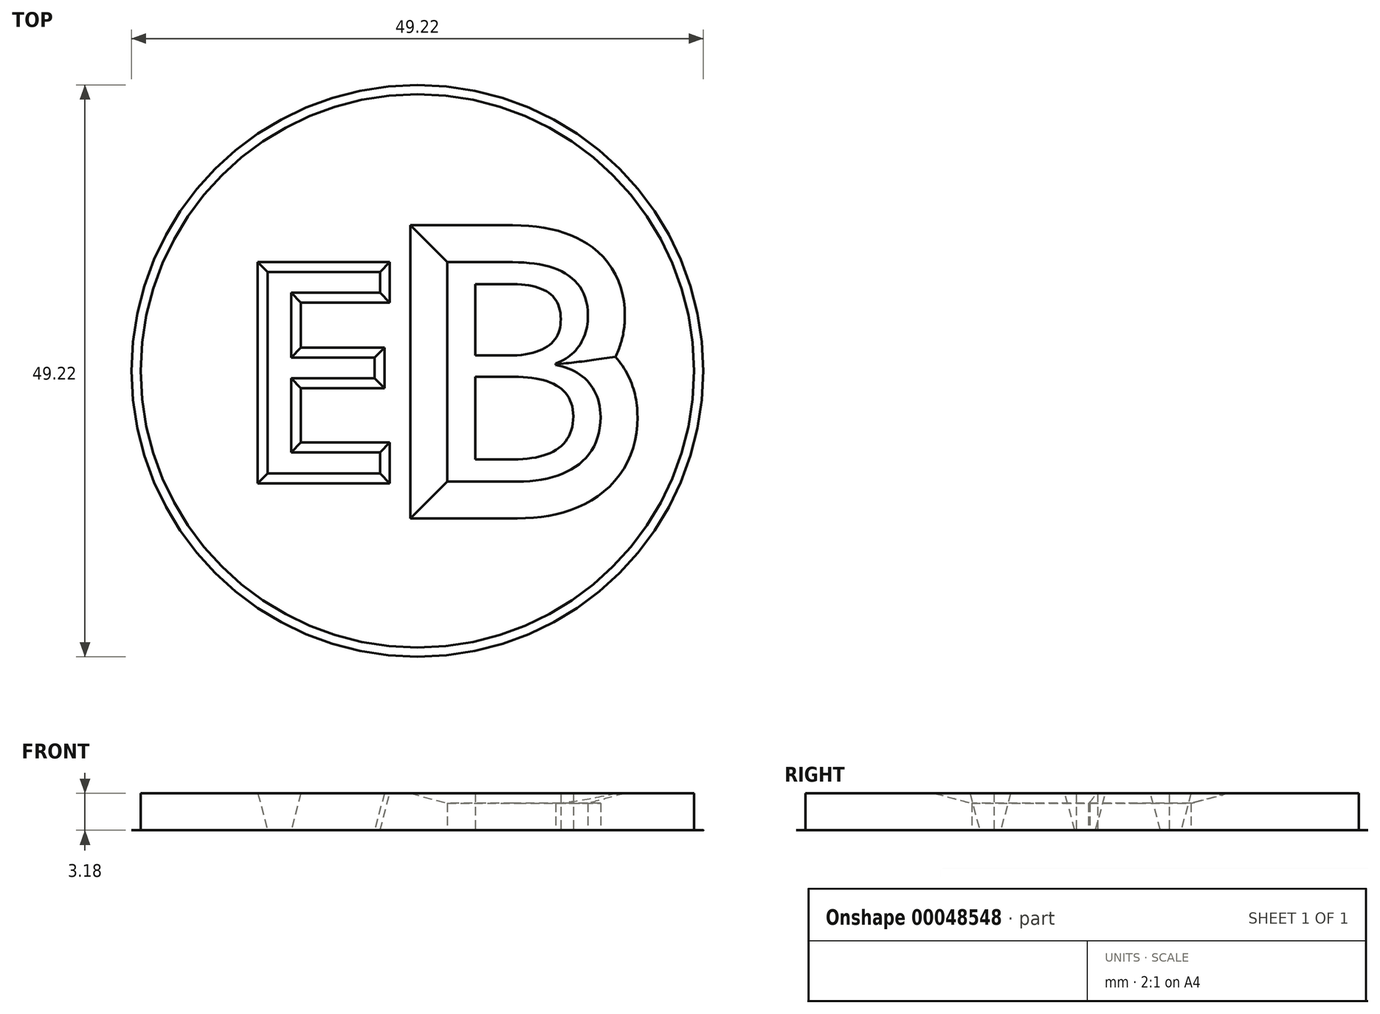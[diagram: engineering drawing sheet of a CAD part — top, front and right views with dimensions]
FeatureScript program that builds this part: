
annotation { "Feature Type Name" : "Feature", "Feature Type Description" : "" }
export const myFeature = defineFeature(function(context is Context, id is Id, definition is map)
    precondition{}
    {
        {
            var Q0;
            Q0=qCreatedBy(makeId("Top.planeOp"),FACE);
            var sketch = newSketch(context, id + "F0", { "sketchPlane" : qUnion([Q0])});
            skCircle(sketch, "E0", {"center": v(0, 0) * mm, "radius": 24.6 * mm});
            skSolve(sketch);
        }
        {
            var Q0;
            Q0=makeQuery(id+"F0.imprint","IMPRINT",FACE,{"disambiguationData":[TD([[makeQuery(id+"F0.imprint","IMPRINT",EDGE,{"derivedFrom":sQuery(id+"F0.wireOp",EDGE,"E0")}),1.0]])]});
            extrude(context, id + "F1", {"entities" : qUnion([Q0]), "depth" : 1 / 406.4 * mm});
        }
        {
            var Q0;
            Q0=qCreatedBy(makeId("Top.planeOp"),FACE);
            var sketch = newSketch(context, id + "F2", { "sketchPlane" : qUnion([Q0])});
            skCircle(sketch, "E1", {"center": v(0, 0) * mm, "radius": 23.81 * mm});
            skSolve(sketch);
        }
        {
            var Q0;
            Q0=qSketchRegion(id+"F2",true);
            extrude(context, id + "F3", {"entities" : qUnion([Q0]), "operationType" : NewBodyOperationType.ADD, "depth" : 3.17 * mm});
        }
        {
            var Q0;
            Q0=qCreatedBy(makeId("Top.planeOp"),FACE);
            var sketch = newSketch(context, id + "F4", { "sketchPlane" : qUnion([Q0])});
            skText(sketch, "E2", { "text": "E", "fontName": "OpenSans-Regular.ttf"});
            const initialGuessF4  = {"E2": [-0.01527, -0.00882, 1, 0, 0.01748]};
            skSetInitialGuess(sketch, initialGuessF4);
            skSolve(sketch);
        }
        {
            var Q0;
            Q0=qSketchRegion(id+"F4",true);
            var Q1;
            Q1=qSketchRegion(id+"Fgxxi4QDRaKe19X_1",true);
            extrude(context, id + "F5", {"entities" : qUnion([Q0, Q1]), "operationType" : NewBodyOperationType.REMOVE, "endBound" : BoundingType.THROUGH_ALL, "depth" : 25.4 * mm});
        }
        {
            var Q0;
            Q0=makeQuery(id+"F5.boolean.opBoolean","INTERSECT",EDGE,{"derivedFrom":[makeQuery(id+"F3.opExtrude","CAP_FACE",FACE,{"disambiguationData":[OSD([sQuery(id+"F2.wireOp",EDGE,"E1")])],"isStart":false}),makeQuery(id+"F5.opExtrude","SWEPT_FACE",FACE,{"disambiguationData":[OSD([sQuery(id+"F4.wireOp",EDGE,"E2.sketch_text.stroke-4")])]})]});
            var Q1;
            Q1=makeQuery(id+"F5.boolean.opBoolean","INTERSECT",EDGE,{"derivedFrom":[makeQuery(id+"F3.opExtrude","CAP_FACE",FACE,{"disambiguationData":[OSD([sQuery(id+"F2.wireOp",EDGE,"E1")])],"isStart":false}),makeQuery(id+"F5.opExtrude","SWEPT_FACE",FACE,{"disambiguationData":[OSD([sQuery(id+"F4.wireOp",EDGE,"E2.sketch_text.stroke-2")])]})]});
            var Q2;
            Q2=makeQuery(id+"F5.boolean.opBoolean","INTERSECT",EDGE,{"derivedFrom":[makeQuery(id+"F3.opExtrude","CAP_FACE",FACE,{"disambiguationData":[OSD([sQuery(id+"F2.wireOp",EDGE,"E1")])],"isStart":false}),makeQuery(id+"F5.opExtrude","SWEPT_FACE",FACE,{"disambiguationData":[OSD([sQuery(id+"F4.wireOp",EDGE,"E2.sketch_text.stroke-1")])]})]});
            var Q3;
            Q3=makeQuery(id+"F5.boolean.opBoolean","INTERSECT",EDGE,{"derivedFrom":[makeQuery(id+"F3.opExtrude","CAP_FACE",FACE,{"disambiguationData":[OSD([sQuery(id+"F2.wireOp",EDGE,"E1")])],"isStart":false}),makeQuery(id+"F5.opExtrude","SWEPT_FACE",FACE,{"disambiguationData":[OSD([sQuery(id+"F4.wireOp",EDGE,"E2.sketch_text.stroke-8")])]})]});
            var Q4;
            Q4=makeQuery(id+"F5.boolean.opBoolean","INTERSECT",EDGE,{"derivedFrom":[makeQuery(id+"F3.opExtrude","CAP_FACE",FACE,{"disambiguationData":[OSD([sQuery(id+"F2.wireOp",EDGE,"E1")])],"isStart":false}),makeQuery(id+"F5.opExtrude","SWEPT_FACE",FACE,{"disambiguationData":[OSD([sQuery(id+"F4.wireOp",EDGE,"E2.sketch_text.stroke-0")])]})]});
            var Q5;
            Q5=makeQuery(id+"F5.boolean.opBoolean","INTERSECT",EDGE,{"derivedFrom":[makeQuery(id+"F3.opExtrude","CAP_FACE",FACE,{"disambiguationData":[OSD([sQuery(id+"F2.wireOp",EDGE,"E1")])],"isStart":false}),makeQuery(id+"F5.opExtrude","SWEPT_FACE",FACE,{"disambiguationData":[OSD([sQuery(id+"F4.wireOp",EDGE,"E2.sketch_text.stroke-10")])]})]});
            var Q6;
            Q6=makeQuery(id+"F5.boolean.opBoolean","INTERSECT",EDGE,{"derivedFrom":[makeQuery(id+"F3.opExtrude","CAP_FACE",FACE,{"disambiguationData":[OSD([sQuery(id+"F2.wireOp",EDGE,"E1")])],"isStart":false}),makeQuery(id+"F5.opExtrude","SWEPT_FACE",FACE,{"disambiguationData":[OSD([sQuery(id+"F4.wireOp",EDGE,"E2.sketch_text.stroke-6")])]})]});
            var Q7;
            Q7=makeQuery(id+"F5.boolean.opBoolean","INTERSECT",EDGE,{"derivedFrom":[makeQuery(id+"F3.opExtrude","CAP_FACE",FACE,{"disambiguationData":[OSD([sQuery(id+"F2.wireOp",EDGE,"E1")])],"isStart":false}),makeQuery(id+"F5.opExtrude","SWEPT_FACE",FACE,{"disambiguationData":[OSD([sQuery(id+"F4.wireOp",EDGE,"E2.sketch_text.stroke-5")])]})]});
            var Q8;
            Q8=makeQuery(id+"F5.boolean.opBoolean","INTERSECT",EDGE,{"derivedFrom":[makeQuery(id+"F3.opExtrude","CAP_FACE",FACE,{"disambiguationData":[OSD([sQuery(id+"F2.wireOp",EDGE,"E1")])],"isStart":false}),makeQuery(id+"F5.opExtrude","SWEPT_FACE",FACE,{"disambiguationData":[OSD([sQuery(id+"F4.wireOp",EDGE,"E2.sketch_text.stroke-9")])]})]});
            var Q9;
            Q9=makeQuery(id+"F5.boolean.opBoolean","INTERSECT",EDGE,{"derivedFrom":[makeQuery(id+"F3.opExtrude","CAP_FACE",FACE,{"disambiguationData":[OSD([sQuery(id+"F2.wireOp",EDGE,"E1")])],"isStart":false}),makeQuery(id+"F5.opExtrude","SWEPT_FACE",FACE,{"disambiguationData":[OSD([sQuery(id+"F4.wireOp",EDGE,"E2.sketch_text.stroke-11")])]})]});
            var Q10;
            Q10=makeQuery(id+"F5.boolean.opBoolean","INTERSECT",EDGE,{"derivedFrom":[makeQuery(id+"F3.opExtrude","CAP_FACE",FACE,{"disambiguationData":[OSD([sQuery(id+"F2.wireOp",EDGE,"E1")])],"isStart":false}),makeQuery(id+"F5.opExtrude","SWEPT_FACE",FACE,{"disambiguationData":[OSD([sQuery(id+"F4.wireOp",EDGE,"E2.sketch_text.stroke-7")])]})]});
            var Q11;
            Q11=makeQuery(id+"F5.boolean.opBoolean","INTERSECT",EDGE,{"derivedFrom":[makeQuery(id+"F3.opExtrude","CAP_FACE",FACE,{"disambiguationData":[OSD([sQuery(id+"F2.wireOp",EDGE,"E1")])],"isStart":false}),makeQuery(id+"F5.opExtrude","SWEPT_FACE",FACE,{"disambiguationData":[OSD([sQuery(id+"F4.wireOp",EDGE,"E2.sketch_text.stroke-3")])]})]});
            chamfer(context, id + "F6", {"entities" : qUnion([Q0, Q1, Q2, Q3, Q4, Q5, Q6, Q7, Q8, Q9, Q10, Q11]), "chamferType" : ChamferType.OFFSET_ANGLE, "width" : 3.17 * mm, "oppositeDirection" : false, "angle" : 15 * degree, "tangentPropagation" : true});
        }
        {
            var Q0;
            Q0=qCreatedBy(makeId("Top.planeOp"),FACE);
            var sketch = newSketch(context, id + "F7", { "sketchPlane" : qUnion([Q0])});
            skText(sketch, "E3", { "text": "B", "fontName": "NotoSansCJKjp-Regular.otf"});
            const initialGuessF7  = {"E3": [0, -0.00952, 1, 0, 0.01854]};
            skSetInitialGuess(sketch, initialGuessF7);
            skSolve(sketch);
        }
        {
            var Q0;
            Q0 = qSketchRegion(id + "F7", true);
            extrude(context, id + "F8", {"entities" : qUnion([Q0]), "operationType" : NewBodyOperationType.REMOVE, "endBound" : BoundingType.THROUGH_ALL, "depth" : 3.17 * mm});
        }
        {
            var Q0;
            Q0=makeQuery(id+"F8.boolean.opBoolean","INTERSECT",EDGE,{"derivedFrom":[makeQuery(id+"F3.opExtrude","CAP_FACE",FACE,{"disambiguationData":[OSD([sQuery(id+"F2.wireOp",EDGE,"E1")])],"isStart":false}),makeQuery(id+"F8.opExtrude","SWEPT_FACE",FACE,{"disambiguationData":[OSD([sQuery(id+"F7.wireOp",EDGE,"E3.sketch_text.stroke-5")])]})]});
            var Q1;
            Q1=makeQuery(id+"F8.boolean.opBoolean","INTERSECT",EDGE,{"derivedFrom":[makeQuery(id+"F3.opExtrude","CAP_FACE",FACE,{"disambiguationData":[OSD([sQuery(id+"F2.wireOp",EDGE,"E1")])],"isStart":false}),makeQuery(id+"F8.opExtrude","SWEPT_FACE",FACE,{"disambiguationData":[OSD([sQuery(id+"F7.wireOp",EDGE,"E3.sketch_text.stroke-6")])]})]});
            var Q2;
            Q2=makeQuery(id+"F8.boolean.opBoolean","INTERSECT",EDGE,{"derivedFrom":[makeQuery(id+"F3.opExtrude","CAP_FACE",FACE,{"disambiguationData":[OSD([sQuery(id+"F2.wireOp",EDGE,"E1")])],"isStart":false}),makeQuery(id+"F8.opExtrude","SWEPT_FACE",FACE,{"disambiguationData":[OSD([sQuery(id+"F7.wireOp",EDGE,"E3.sketch_text.stroke-7")])]})]});
            var Q3;
            Q3=makeQuery(id+"F8.boolean.opBoolean","INTERSECT",EDGE,{"derivedFrom":[makeQuery(id+"F3.opExtrude","CAP_FACE",FACE,{"disambiguationData":[OSD([sQuery(id+"F2.wireOp",EDGE,"E1")])],"isStart":false}),makeQuery(id+"F8.opExtrude","SWEPT_FACE",FACE,{"disambiguationData":[OSD([sQuery(id+"F7.wireOp",EDGE,"E3.sketch_text.stroke-8")])]})]});
            var Q4;
            Q4=makeQuery(id+"F8.boolean.opBoolean","INTERSECT",EDGE,{"derivedFrom":[makeQuery(id+"F3.opExtrude","CAP_FACE",FACE,{"disambiguationData":[OSD([sQuery(id+"F2.wireOp",EDGE,"E1")])],"isStart":false}),makeQuery(id+"F8.opExtrude","SWEPT_FACE",FACE,{"disambiguationData":[OSD([sQuery(id+"F7.wireOp",EDGE,"E3.sketch_text.stroke-10")])]})]});
            var Q5;
            Q5=makeQuery(id+"F8.boolean.opBoolean","INTERSECT",EDGE,{"derivedFrom":[makeQuery(id+"F3.opExtrude","CAP_FACE",FACE,{"disambiguationData":[OSD([sQuery(id+"F2.wireOp",EDGE,"E1")])],"isStart":false}),makeQuery(id+"F8.opExtrude","SWEPT_FACE",FACE,{"disambiguationData":[OSD([sQuery(id+"F7.wireOp",EDGE,"E3.sketch_text.stroke-9")])]})]});
            var Q6;
            Q6=makeQuery(id+"F8.boolean.opBoolean","INTERSECT",EDGE,{"derivedFrom":[makeQuery(id+"F3.opExtrude","CAP_FACE",FACE,{"disambiguationData":[OSD([sQuery(id+"F2.wireOp",EDGE,"E1")])],"isStart":false}),makeQuery(id+"F8.opExtrude","SWEPT_FACE",FACE,{"disambiguationData":[OSD([sQuery(id+"F7.wireOp",EDGE,"E3.sketch_text.stroke-11")])]})]});
            var Q7;
            Q7=makeQuery(id+"F8.boolean.opBoolean","INTERSECT",EDGE,{"derivedFrom":[makeQuery(id+"F3.opExtrude","CAP_FACE",FACE,{"disambiguationData":[OSD([sQuery(id+"F2.wireOp",EDGE,"E1")])],"isStart":false}),makeQuery(id+"F8.opExtrude","SWEPT_FACE",FACE,{"disambiguationData":[OSD([sQuery(id+"F7.wireOp",EDGE,"E3.sketch_text.stroke-12")])]})]});
            var Q8;
            Q8=makeQuery(id+"F8.boolean.opBoolean","INTERSECT",EDGE,{"derivedFrom":[makeQuery(id+"F3.opExtrude","CAP_FACE",FACE,{"disambiguationData":[OSD([sQuery(id+"F2.wireOp",EDGE,"E1")])],"isStart":false}),makeQuery(id+"F8.opExtrude","SWEPT_FACE",FACE,{"disambiguationData":[OSD([sQuery(id+"F7.wireOp",EDGE,"E3.sketch_text.stroke-4")])]})]});
            var Q9;
            Q9=makeQuery(id+"F8.boolean.opBoolean","INTERSECT",EDGE,{"derivedFrom":[makeQuery(id+"F3.opExtrude","CAP_FACE",FACE,{"disambiguationData":[OSD([sQuery(id+"F2.wireOp",EDGE,"E1")])],"isStart":false}),makeQuery(id+"F8.opExtrude","SWEPT_FACE",FACE,{"disambiguationData":[OSD([sQuery(id+"F7.wireOp",EDGE,"E3.sketch_text.stroke-2")])]})]});
            var Q10;
            Q10=makeQuery(id+"F8.boolean.opBoolean","INTERSECT",EDGE,{"derivedFrom":[makeQuery(id+"F3.opExtrude","CAP_FACE",FACE,{"disambiguationData":[OSD([sQuery(id+"F2.wireOp",EDGE,"E1")])],"isStart":false}),makeQuery(id+"F8.opExtrude","SWEPT_FACE",FACE,{"disambiguationData":[OSD([sQuery(id+"F7.wireOp",EDGE,"E3.sketch_text.stroke-1")])]})]});
            var Q11;
            Q11=makeQuery(id+"F8.boolean.opBoolean","INTERSECT",EDGE,{"derivedFrom":[makeQuery(id+"F3.opExtrude","CAP_FACE",FACE,{"disambiguationData":[OSD([sQuery(id+"F2.wireOp",EDGE,"E1")])],"isStart":false}),makeQuery(id+"F8.opExtrude","SWEPT_FACE",FACE,{"disambiguationData":[OSD([sQuery(id+"F7.wireOp",EDGE,"E3.sketch_text.stroke-0")])]})]});
            var Q12;
            Q12=makeQuery(id+"F8.boolean.opBoolean","INTERSECT",EDGE,{"derivedFrom":[makeQuery(id+"F3.opExtrude","CAP_FACE",FACE,{"disambiguationData":[OSD([sQuery(id+"F2.wireOp",EDGE,"E1")])],"isStart":false}),makeQuery(id+"F8.opExtrude","SWEPT_FACE",FACE,{"disambiguationData":[OSD([sQuery(id+"F7.wireOp",EDGE,"E3.sketch_text.stroke-17")])]})]});
            var Q13;
            Q13=makeQuery(id+"F8.boolean.opBoolean","INTERSECT",EDGE,{"derivedFrom":[makeQuery(id+"F3.opExtrude","CAP_FACE",FACE,{"disambiguationData":[OSD([sQuery(id+"F2.wireOp",EDGE,"E1")])],"isStart":false}),makeQuery(id+"F8.opExtrude","SWEPT_FACE",FACE,{"disambiguationData":[OSD([sQuery(id+"F7.wireOp",EDGE,"E3.sketch_text.stroke-16")])]})]});
            var Q14;
            Q14=makeQuery(id+"F8.boolean.opBoolean","INTERSECT",EDGE,{"derivedFrom":[makeQuery(id+"F3.opExtrude","CAP_FACE",FACE,{"disambiguationData":[OSD([sQuery(id+"F2.wireOp",EDGE,"E1")])],"isStart":false}),makeQuery(id+"F8.opExtrude","SWEPT_FACE",FACE,{"disambiguationData":[OSD([sQuery(id+"F7.wireOp",EDGE,"E3.sketch_text.stroke-15")])]})]});
            var Q15;
            Q15=makeQuery(id+"F8.boolean.opBoolean","SPLIT",FACE,{"disambiguationData":[TD([makeQuery(id+"F8.opExtrude","SWEPT_FACE",FACE,{"disambiguationData":[OSD([sQuery(id+"F7.wireOp",EDGE,"E3.sketch_text.stroke-13")])]})])],"derivedFrom":makeQuery(id+"F3.opExtrude","CAP_FACE",FACE,{"disambiguationData":[OSD([sQuery(id+"F2.wireOp",EDGE,"E1")])],"isStart":false})});
            var Q16;
            Q16=makeQuery(id+"F8.boolean.opBoolean","INTERSECT",EDGE,{"derivedFrom":[makeQuery(id+"F3.opExtrude","CAP_FACE",FACE,{"disambiguationData":[OSD([sQuery(id+"F2.wireOp",EDGE,"E1")])],"isStart":false}),makeQuery(id+"F8.opExtrude","SWEPT_FACE",FACE,{"disambiguationData":[OSD([sQuery(id+"F7.wireOp",EDGE,"E3.sketch_text.stroke-14")])]})]});
            var Q17;
            Q17=makeQuery(id+"F8.boolean.opBoolean","INTERSECT",EDGE,{"derivedFrom":[makeQuery(id+"F3.opExtrude","CAP_FACE",FACE,{"disambiguationData":[OSD([sQuery(id+"F2.wireOp",EDGE,"E1")])],"isStart":false}),makeQuery(id+"F8.opExtrude","SWEPT_FACE",FACE,{"disambiguationData":[OSD([sQuery(id+"F7.wireOp",EDGE,"E3.sketch_text.stroke-13")])]})]});
            chamfer(context, id + "F9", {"entities" : qUnion([Q0, Q1, Q2, Q3, Q4, Q5, Q6, Q7, Q8, Q9, Q10, Q11, Q12, Q13, Q14, Q15, Q16, Q17]), "chamferType" : ChamferType.OFFSET_ANGLE, "width" : 3.17 * mm, "oppositeDirection" : false, "angle" : 15 * degree, "tangentPropagation" : true});
        }
    });
